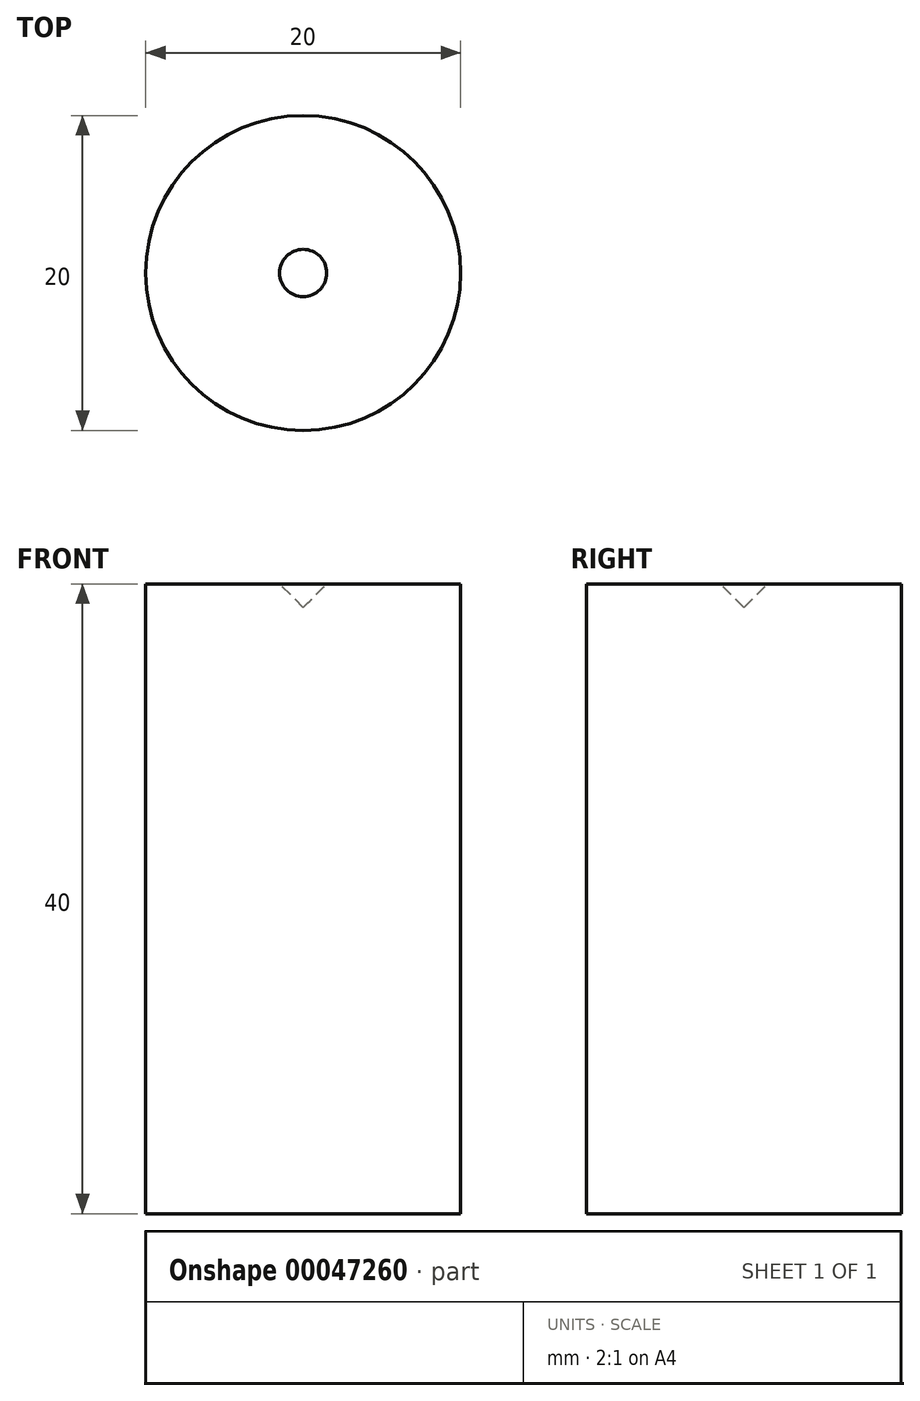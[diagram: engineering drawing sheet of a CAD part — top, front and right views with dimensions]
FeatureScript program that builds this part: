
annotation { "Feature Type Name" : "Feature", "Feature Type Description" : "" }
export const myFeature = defineFeature(function(context is Context, id is Id, definition is map)
    precondition{}
    {
        {
            var Q0;
            Q0=qCreatedBy(makeId("Top.planeOp"),FACE);
            var sketch = newSketch(context, id + "F0", { "sketchPlane" : qUnion([Q0])});
            skCircle(sketch, "E0", {"center": v(0, 0) * mm, "radius": 10 * mm});
            skSolve(sketch);
        }
        {
            var Q0;
            Q0 = qSketchRegion(id + "F0", true);
            extrude(context, id + "F1", {"entities" : qUnion([Q0]), "depth" : 40 * mm});
        }
        {
            var Q0;
            Q0=makeQuery(id+"F1.opExtrude","CAP_FACE",FACE,{"disambiguationData":[OSD([sQuery(id+"F0.wireOp",EDGE,"E0")])],"isStart":false});
            var sketch = newSketch(context, id + "F2", { "sketchPlane" : qUnion([Q0])});
            skCircle(sketch, "E1", {"center": v(0, 0) * mm, "radius": 1.5 * mm});
            skSolve(sketch);
        }
        {
            var Q0;
            Q0 = qSketchRegion(id + "F2", true);
            extrude(context, id + "F3", {"entities" : qUnion([Q0]), "operationType" : NewBodyOperationType.REMOVE, "oppositeDirection" : true, "depth" : 1.5 * mm});
        }
        {
            var Q0;
            Q0=makeQuery(id+"F3.boolean.opBoolean","COPY",EDGE,{"derivedFrom":makeQuery(id+"F3.opExtrude","CAP_EDGE",EDGE,{"disambiguationData":[OSD([sQuery(id+"F2.wireOp",EDGE,"E1")])],"isStart":false})});
            chamfer(context, id + "F4", {"entities" : qUnion([Q0]), "width" : 1.5 * mm, "tangentPropagation" : true});
        }
    });
